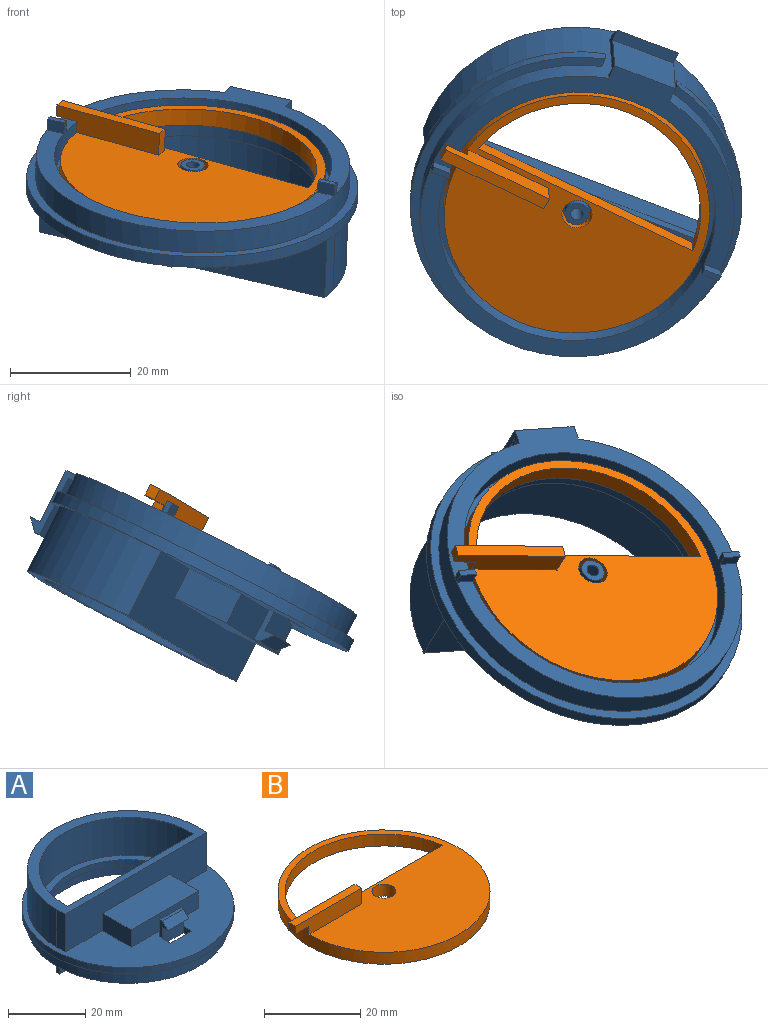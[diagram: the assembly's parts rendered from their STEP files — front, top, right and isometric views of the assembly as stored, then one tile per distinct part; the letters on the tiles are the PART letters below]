
ASSEMBLY  parts=2 mates=1
PART A: 52 faces, bbox 54.9x57.4x20 mm
  f0: plane 5.5x3mm, normal (1,0,0), area 7.5mm2, adj f1,f7,f17,f30,f50,f51
  f1: plane 7.65x1mm, normal (0,0,1), area 7.7mm2, adj f0,f13,f50,f51
  f2: plane 52x27.91mm, normal (0,0,-1), area 254.1mm2, adj f5,f29,f31,f32,f35,f44,f48
  f3: plane 51.96x25mm, normal (0,0,-1), area 224.9mm2, adj f5,f29,f42,f47
  f4: plane 0.64x0.05mm, normal (0,0,-1), area 0mm2, adj f8,f40
  f5: cylinder r=26mm len=52mm, axis (0,0,-1), area 1684.9mm2, adj f2,f3,f6,f9,f11,f17,f21,f23
  f6: cylinder r=26mm len=12mm, axis (0,0,-1), area 36.1mm2, adj f5,f9,f11,f17
  f7: plane 7.65x5.5mm, normal (0,-1,0), area 42.1mm2, adj f0,f13,f18,f24,f25,f30
  f8: plane 45.96x12mm, normal (0,1,0), area 551.5mm2, adj f4,f10,f11,f28
  f9: plane 51.65x12mm, normal (0,-1,0), area 484.2mm2, adj f5,f6,f11,f14,f15,f16,f17
  f10: cylinder r=23mm len=46mm, axis (0,0,-1), area 891.1mm2, adj f8,f11,f28
  f11: plane 52x29mm, normal (0,0,1), area 340.6mm2, adj f5,f6,f8,f9,f10
  f12: plane 24.65x5.5mm, normal (0,-1,0), area 135.6mm2, adj f14,f15,f16,f17
  f13: plane 5.5x3mm, normal (-1,0,0), area 7.5mm2, adj f1,f7,f17,f30,f50,f51
  f14: plane 10.5x5.5mm, normal (1,0,0), area 57.7mm2, adj f9,f12,f16,f17
  f15: plane 10.5x5.5mm, normal (-1,0,0), area 57.7mm2, adj f9,f12,f16,f17
  f16: plane 24.65x10.5mm, normal (0,0,1), area 258.9mm2, adj f9,f12,f14,f15
  f17: plane 54.94x54.16mm, normal (0,0,1), area 844mm2, adj f0,f5,f6,f9,f12,f13,f14,f15
  f18: plane 46x46mm, normal (0,0,-1), area 1017.5mm2, adj f7,f19,f20,f24,f25,f26,f29,f39
  f19: plane 41.81x2mm, normal (0,1,0), area 83.6mm2, adj f18,f20,f28
  f20: cylinder r=21mm len=41.81mm, axis (0,0,1), area 123.9mm2, adj f18,f19,f28
  f21: plane 2x1.51mm, normal (1,0,0), area 3mm2, adj f5,f17,f22,f27
  f22: cylinder r=27.47mm len=54.94mm, axis (0,0,1), area 318.9mm2, adj f17,f21,f23,f27
  f23: plane 2x1.51mm, normal (-1,0,0), area 3mm2, adj f5,f17,f22,f27
  f24: plane 3x2mm, normal (1,0,0), area 6mm2, adj f7,f17,f18,f26
  f25: plane 3x2mm, normal (-1,0,0), area 6mm2, adj f7,f17,f18,f26
  f26: plane 7.65x2mm, normal (0,1,0), area 15.3mm2, adj f17,f18,f24,f25
  f27: plane 54.94x54.16mm, normal (0,0,-1), area 227.3mm2, adj f5,f21,f22,f23
  f28: plane 46x24mm, normal (0,0,1), area 264.6mm2, adj f8,f10,f19,f20,f40
  f29: cylinder r=23mm len=46mm, axis (0,0,1), area 582.1mm2, adj f2,f3,f18,f42,f44,f45,f47,f48
  f30: plane 7.65x2mm, normal (0,0,-1), area 15.3mm2, adj f0,f7,f13,f50
  f31: plane 11.5x4.5mm, normal (1,0,0), area 15mm2, adj f2,f5,f33,f34,f35,f36,f37,f38
  f32: plane 11.5x4.5mm, normal (-1,0,0), area 15mm2, adj f2,f5,f33,f34,f35,f36,f37,f38
  f33: plane 11x1.5mm, normal (0,0,1), area 12.2mm2, adj f5,f31,f32,f34
  f34: plane 11x10.5mm, normal (0,-1,0), area 115.5mm2, adj f31,f32,f33,f36
  f35: plane 11x9.5mm, normal (0,1,0), area 104.5mm2, adj f2,f31,f32,f37
  f36: plane 11x1mm, normal (0,0,1), area 11mm2, adj f31,f32,f34,f38
  f37: plane 11x2mm, normal (0,0,-1), area 22mm2, adj f31,f32,f35,f38
  f38: plane 11x2mm, normal (0,0.71,0.71), area 31.1mm2, adj f31,f32,f36,f37
  f39: cylinder r=2mm len=4mm, axis (0,0,1), area 40.2mm2, adj f18,f41
  f40: cylinder r=1.05mm len=5.2mm, axis (0,0,1), area 34.3mm2, adj f4,f28,f41
  f41: plane 4x4mm, normal (0,0,-1), area 9.1mm2, adj f39,f40
  f42: plane 3x2mm, normal (0,-1,0), area 6mm2, adj f3,f29,f43,f45
  f43: plane 2.01x1.01mm, normal (-1,-0.02,0), area 2mm2, adj f5,f42,f44,f45
  f44: plane 3x2mm, normal (0,1,0), area 6mm2, adj f2,f29,f43,f45
  f45: plane 3.02x1mm, normal (0,0,-1), area 3mm2, adj f29,f42,f43,f44
  f46: plane 2.01x1.01mm, normal (1,-0.02,0), area 2mm2, adj f5,f47,f48,f49
  f47: plane 3x2mm, normal (0,-1,0), area 6mm2, adj f3,f29,f46,f49
  f48: plane 3x2mm, normal (0,1,0), area 6mm2, adj f2,f29,f46,f49
  f49: plane 3.02x1mm, normal (0,0,-1), area 3mm2, adj f29,f46,f47,f48
  f50: plane 7.65x2mm, normal (0,-0.71,0.71), area 21.6mm2, adj f0,f1,f13,f30
  f51: plane 7.65x5.5mm, normal (0,1,0), area 42.1mm2, adj f0,f1,f13,f17
PART B: 12 faces, bbox 47.9x44x7 mm
  f0: plane 19.42x4mm, normal (0,-1,0), area 69.8mm2, adj f1,f5,f8,f9,f10,f11
  f1: plane 44x44mm, normal (0,0,1), area 932.4mm2, adj f0,f2,f3,f4,f5,f7,f9
  f2: plane 40.56x3mm, normal (0,1,0), area 121.7mm2, adj f1,f3,f6
  f3: cylinder r=20.5mm len=40.56mm, axis (0,0,-1), area 175.1mm2, adj f1,f2,f6
  f4: cylinder r=2.5mm len=5mm, axis (0,0,-1), area 47.1mm2, adj f1,f6
  f5: cylinder r=22mm len=44mm, axis (0,0,-1), area 418.7mm2, adj f0,f1,f6,f7,f11
  f6: plane 44x44mm, normal (0,0,-1), area 963.3mm2, adj f2,f3,f4,f5
  f7: plane 19.42x4mm, normal (0,1,0), area 69.7mm2, adj f1,f5,f8,f9,f10,f11
  f8: plane 2x2mm, normal (-1,0,0), area 4mm2, adj f0,f7,f10,f11
  f9: plane 4x2mm, normal (1,0,0), area 8mm2, adj f0,f1,f7,f10
  f10: plane 19.42x2mm, normal (0,0,1), area 38.8mm2, adj f0,f7,f8,f9
  f11: plane 4.01x2mm, normal (0,0,-1), area 7.9mm2, adj f0,f5,f7,f8
PLACE A rot(axis=(-0.2,-0.95,-0.22),172.6deg) t=(-50.73,30.17,-23.95)mm
PLACE B rot(axis=(0.66,0.22,-0.72),38.8deg) t=(-50.65,29.19,-21.99)mm
MATE revolute A.f5 <-> B.f3  axis (0.04,-0.45,0.89) through (-50.54,27.84,-19.31)mm
